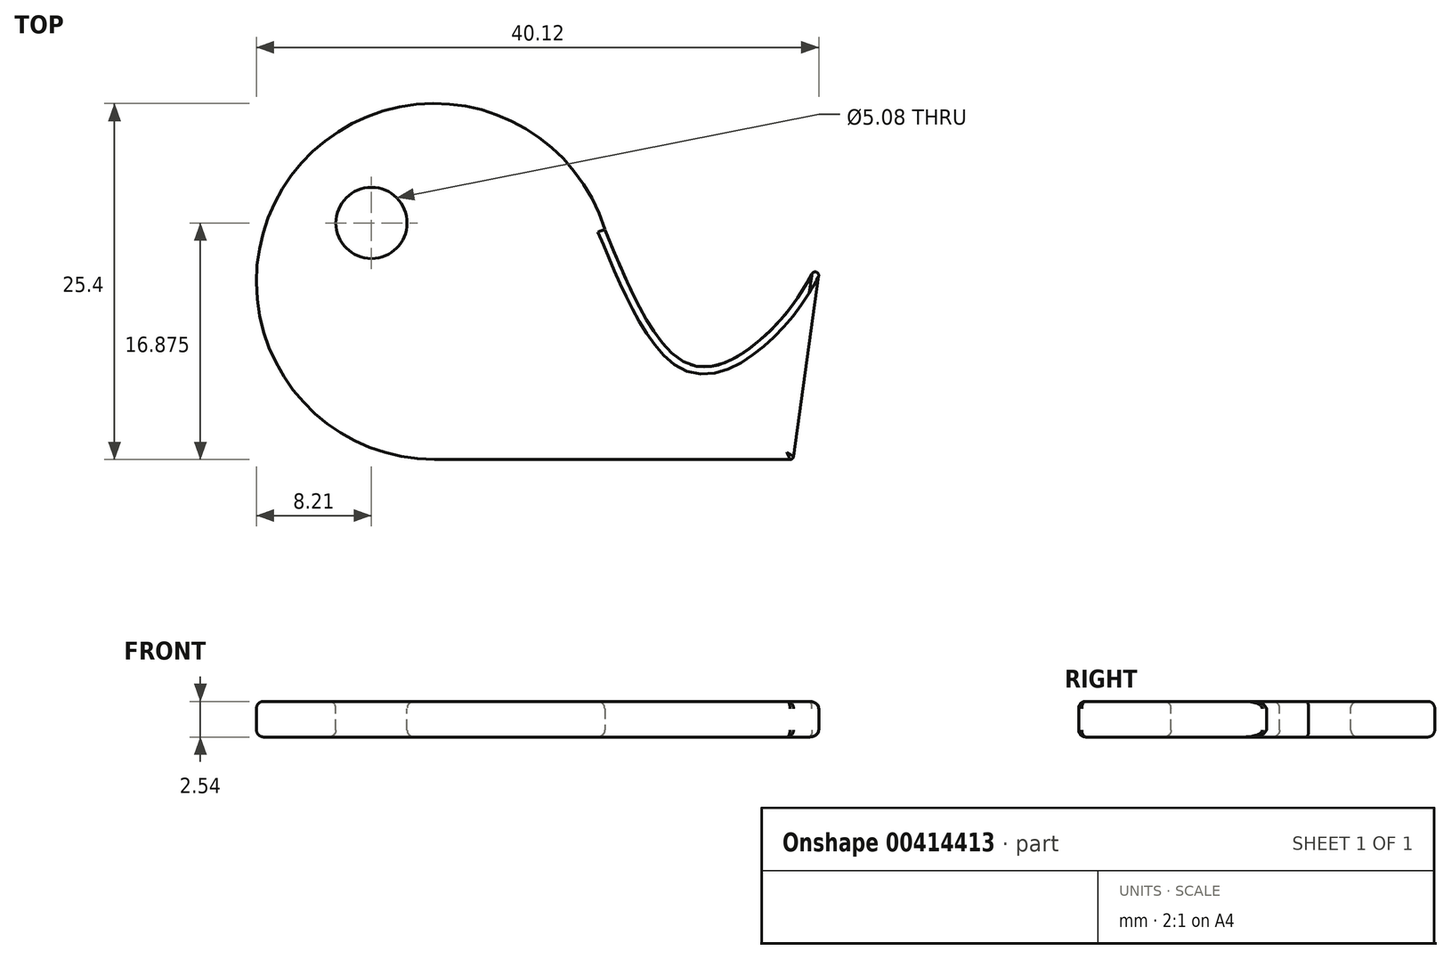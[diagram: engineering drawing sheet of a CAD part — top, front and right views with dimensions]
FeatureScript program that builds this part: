
annotation { "Feature Type Name" : "Feature", "Feature Type Description" : "" }
export const myFeature = defineFeature(function(context is Context, id is Id, definition is map)
    precondition{}
    {
        {
            var Q0;
            Q0=qCreatedBy(makeId("Top.planeOp"),FACE);
            var sketch = newSketch(context, id + "F0", { "sketchPlane" : qUnion([Q0])});
            skArc(sketch, "E0", {"start": v(12.15, 3.7) * mm, "mid": v(-10.2, 7.56) * mm, "end": v(0, -12.7) * mm});
            skFitSpline(sketch, "E1", {"points": [v(12.15, 3.7) * mm, v(18.6, -6.04) * mm, v(24.7, -2.72) * mm, v(27.63, 1.9) * mm], "startDerivative": vector(14.08, -33.78) * mm, "endDerivative": vector(8.06, 16.2) * mm});
            skLineSegment(sketch, "E2", {"start": v(0, -12.7) * mm, "end": v(25.6, -12.7) * mm});
            skLineSegment(sketch, "E3", {"start": v(25.6, -12.7) * mm, "end": v(27.63, 1.9) * mm});
            skSolve(sketch);
        }
        {
            var Q0;
            Q0=makeQuery(id+"F0.imprint","IMPRINT",FACE,{"disambiguationData":[TD([[makeQuery(id+"F0.imprint","IMPRINT",EDGE,{"derivedFrom":sQuery(id+"F0.wireOp",EDGE,"E0")}),1.0]])]});
            extrude(context, id + "F1", {"entities" : qUnion([Q0]), "depth" : 2.54 * mm});
        }
        {
            var Q0;
            Q0=makeQuery(id+"F1.opExtrude","CAP_FACE",FACE,{"disambiguationData":[OSD([sQuery(id+"F0.wireOp",EDGE,"E0"),sQuery(id+"F0.wireOp",EDGE,"E1"),sQuery(id+"F0.wireOp",EDGE,"E2"),sQuery(id+"F0.wireOp",EDGE,"E3")])],"isStart":false});
            var sketch = newSketch(context, id + "F2", { "sketchPlane" : qUnion([Q0])});
            skCircle(sketch, "E4", {"center": v(-4.5, 4.18) * mm, "radius": 2.54 * mm});
            skSolve(sketch);
        }
        {
            var Q0;
            Q0 = qSketchRegion(id + "F2", true);
            extrude(context, id + "F3", {"entities" : qUnion([Q0]), "operationType" : NewBodyOperationType.REMOVE, "oppositeDirection" : true, "depth" : 25.4 * mm});
        }
        {
            var Q0;
            Q0=makeQuery(id+"F1.opExtrude","SWEPT_EDGE",EDGE,{"disambiguationData":[OSD([sQuery(id+"F0.wireOp",EDGE,"E1"),sQuery(id+"F0.wireOp",EDGE,"E3")])]});
            var Q1;
            Q1=makeQuery(id+"F1.opExtrude","SWEPT_EDGE",EDGE,{"disambiguationData":[OSD([sQuery(id+"F0.wireOp",EDGE,"E2"),sQuery(id+"F0.wireOp",EDGE,"E3")])]});
            fillet(context, id + "F4", {"entities" : qUnion([Q0, Q1]), "radius" : 0.25 * mm, "tangentPropagation" : true, "allowEdgeOverflow" : false});
        }
        {
            var Q0;
            Q0=makeQuery(id+"F1.opExtrude","CAP_FACE",FACE,{"disambiguationData":[OSD([sQuery(id+"F0.wireOp",EDGE,"E0"),sQuery(id+"F0.wireOp",EDGE,"E1"),sQuery(id+"F0.wireOp",EDGE,"E2"),sQuery(id+"F0.wireOp",EDGE,"E3")])],"isStart":false});
            var Q1;
            Q1=makeQuery(id+"F1.opExtrude","CAP_FACE",FACE,{"disambiguationData":[OSD([sQuery(id+"F0.wireOp",EDGE,"E0"),sQuery(id+"F0.wireOp",EDGE,"E1"),sQuery(id+"F0.wireOp",EDGE,"E2"),sQuery(id+"F0.wireOp",EDGE,"E3")])],"isStart":true});
            fillet(context, id + "F5", {"entities" : qUnion([Q0, Q1]), "radius" : 0.5 * mm, "tangentPropagation" : true, "allowEdgeOverflow" : false});
        }
    });
